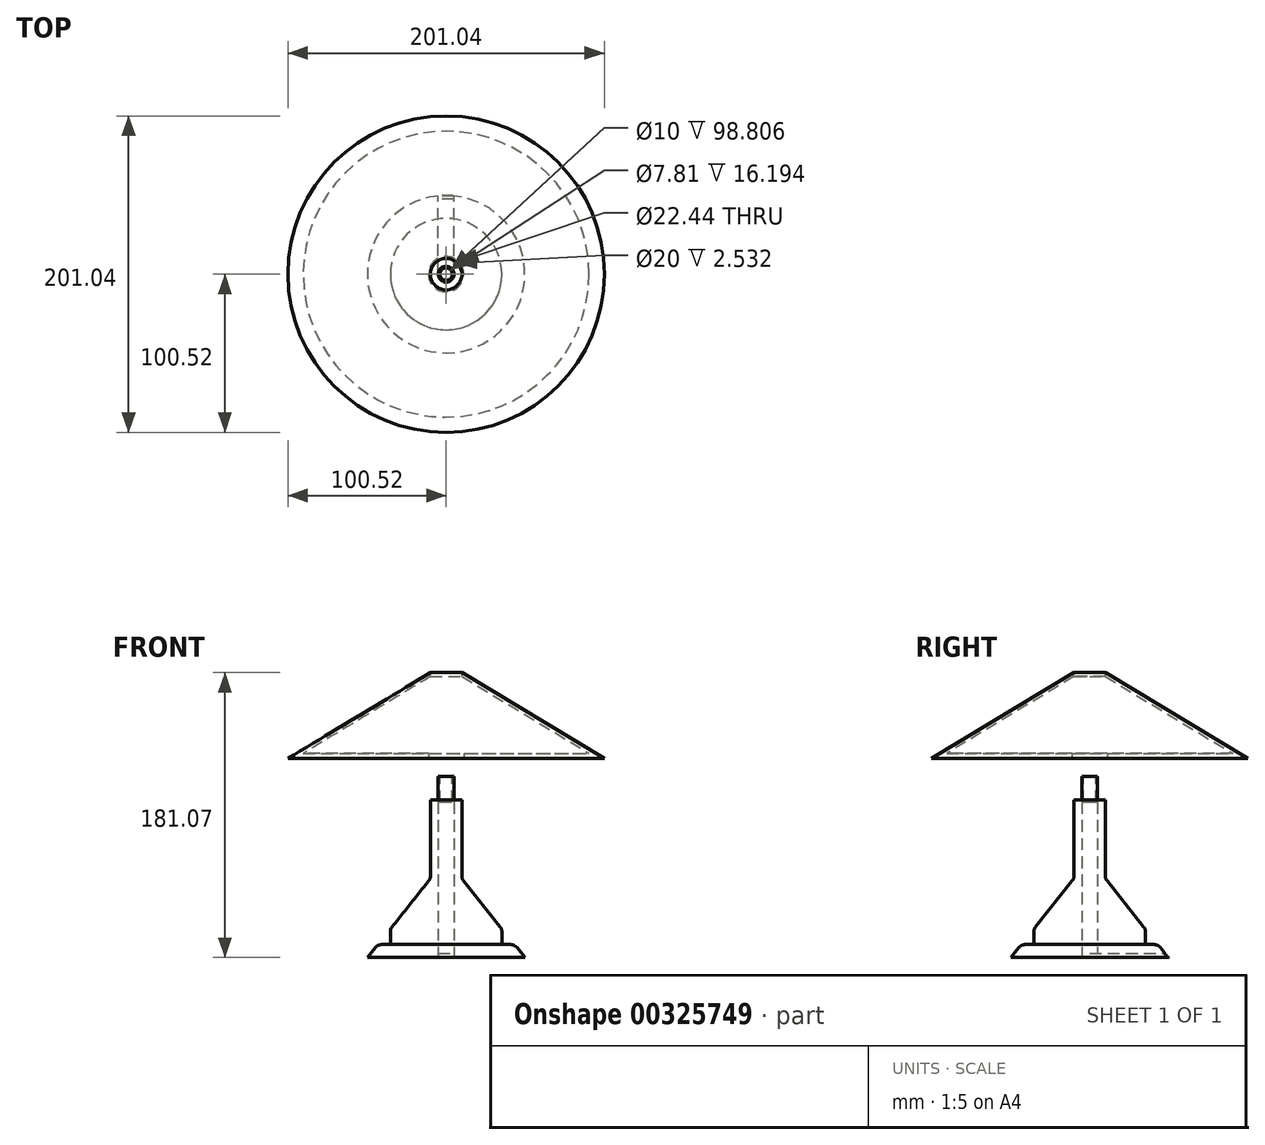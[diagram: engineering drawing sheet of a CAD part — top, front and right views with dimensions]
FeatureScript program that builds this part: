
annotation { "Feature Type Name" : "Feature", "Feature Type Description" : "" }
export const myFeature = defineFeature(function(context is Context, id is Id, definition is map)
    precondition{}
    {
        {
            var Q0;
            Q0=qCreatedBy(makeId("Front.planeOp"),FACE);
            var sketch = newSketch(context, id + "F0", { "sketchPlane" : qUnion([Q0])});
            skLineSegment(sketch, "E0", {"start": v(0, -50) * mm, "end": v(-50, -50) * mm});
            skLineSegment(sketch, "E1", {"start": v(-50, -50) * mm, "end": v(-43.39, -41.73) * mm});
            skLineSegment(sketch, "E2", {"start": v(-10, 0) * mm, "end": v(-10, 50) * mm});
            skLineSegment(sketch, "E3", {"start": v(-10, 50) * mm, "end": v(0, 50) * mm});
            skLineSegment(sketch, "E4", {"start": v(0, 50) * mm, "end": v(0, -50) * mm});
            skLineSegment(sketch, "E5", {"start": v(-5, 50) * mm, "end": v(-5, 65) * mm});
            skLineSegment(sketch, "E6", {"start": v(-5, 65) * mm, "end": v(0, 65) * mm});
            skLineSegment(sketch, "E7", {"start": v(0, 65) * mm, "end": v(0, 50) * mm});
            skLineSegment(sketch, "E8", {"start": v(-43.39, -41.73) * mm, "end": v(-35.4, -41.73) * mm});
            skLineSegment(sketch, "E9", {"start": v(-35.4, -41.73) * mm, "end": v(-35.4, -31.75) * mm});
            skLineSegment(sketch, "E10.trimOffspring", {"start": v(-35.4, -31.75) * mm, "end": v(-10, 0) * mm});
            skSolve(sketch);
        }
        {
            var Q0;
            Q0=qSketchRegion(id+"F0",true);
            var Q1;
            Q1=sQuery(id+"F0.wireOp",EDGE,"E7");
            revolve(context, id + "F1", {"entities" : qUnion([Q0]), "axis" : qUnion([Q1]), "revolveType" : RevolveType.FULL});
        }
        {
            var Q0;
            Q0=makeQuery(id+"F1.opRevolve","SWEPT_FACE",FACE,{"disambiguationData":[OSD([sQuery(id+"F0.wireOp",EDGE,"E0")])]});
            var sketch = newSketch(context, id + "F2", { "sketchPlane" : qUnion([Q0])});
            skCircle(sketch, "E11", {"center": v(0, 0) * mm, "radius": 5 * mm});
            skSolve(sketch);
        }
        {
            var Q0;
            Q0=makeQuery(id+"F2.imprint","IMPRINT",FACE,{"disambiguationData":[TD([[makeQuery(id+"F2.imprint","IMPRINT",EDGE,{"derivedFrom":sQuery(id+"F2.wireOp",EDGE,"E11")}),1.0]])]});
            extrude(context, id + "F3", {"entities" : qUnion([Q0]), "operationType" : NewBodyOperationType.REMOVE, "oppositeDirection" : true, "depth" : 98.8 * mm});
        }
        {
            var Q0;
            Q0=makeQuery(id+"F1.opRevolve","SWEPT_FACE",FACE,{"disambiguationData":[OSD([sQuery(id+"F0.wireOp",EDGE,"E6")])]});
            var sketch = newSketch(context, id + "F4", { "sketchPlane" : qUnion([Q0])});
            skCircle(sketch, "E12", {"center": v(0, 0) * mm, "radius": 3.9 * mm});
            skSolve(sketch);
        }
        {
            var Q0;
            Q0=makeQuery(id+"F4.imprint","IMPRINT",FACE,{"disambiguationData":[TD([[makeQuery(id+"F4.imprint","IMPRINT",EDGE,{"derivedFrom":sQuery(id+"F4.wireOp",EDGE,"E12")}),1.0]])]});
            var Q1;
            Q1=sQuery(id+"F4.wireOp",EDGE,"E12");
            extrude(context, id + "F5", {"entities" : qUnion([Q0]), "operationType" : NewBodyOperationType.REMOVE, "surfaceEntities" : qUnion([Q1]), "oppositeDirection" : true, "depth" : 18.03 * mm});
        }
        {
            var Q0;
            Q0=qCreatedBy(makeId("Front.planeOp"),FACE);
            var sketch = newSketch(context, id + "F6", { "sketchPlane" : qUnion([Q0])});
            skLineSegment(sketch, "E13", {"start": v(0, 81.07) * mm, "end": v(0, 83.72) * mm});
            skLineSegment(sketch, "E14", {"start": v(100.52, 76.39) * mm, "end": v(10, 131.07) * mm});
            skLineSegment(sketch, "E15", {"start": v(0, 131.07) * mm, "end": v(10, 131.07) * mm});
            skLineSegment(sketch, "E16", {"start": v(0, 128.54) * mm, "end": v(10, 128.54) * mm});
            skLineSegment(sketch, "E17", {"start": v(10, 128.54) * mm, "end": v(90.8, 79.72) * mm});
            skLineSegment(sketch, "E18.trimOffspring", {"start": v(0, 128.54) * mm, "end": v(0, 131.07) * mm});
            skLineSegment(sketch, "E19", {"start": v(0, 131.07) * mm, "end": v(0, 81.07) * mm});
            skLineSegment(sketch, "E20", {"start": v(100.52, 76.39) * mm, "end": v(11.22, 76.39) * mm});
            skLineSegment(sketch, "E21", {"start": v(11.22, 76.39) * mm, "end": v(11.22, 79.63) * mm});
            skLineSegment(sketch, "E22", {"start": v(11.22, 79.63) * mm, "end": v(90.8, 79.72) * mm});
            skSolve(sketch);
        }
        {
            var Q0;
            Q0=qSketchRegion(id+"F6",true);
            var Q1;
            Q1=sQuery(id+"F6.wireOp",EDGE,"pKssnT2N-DJuv-aNKx-k4Lw-VZBVBOwzWhS8");
            var Q2;
            Q2=sQuery(id+"F6.wireOp",EDGE,"E16");
            var Q3;
            Q3=sQuery(id+"F6.wireOp",EDGE,"E17");
            var Q4;
            Q4=sQuery(id+"F6.wireOp",EDGE,"MncOqVzV-dVDM-nEzL-s3Sz-IolONIR63Kfi");
            var Q5;
            Q5=sQuery(id+"F6.wireOp",EDGE,"E13");
            revolve(context, id + "F7", {"entities" : qUnion([Q0]), "surfaceEntities" : qUnion([Q1, Q2, Q3, Q4]), "axis" : qUnion([Q5]), "revolveType" : RevolveType.FULL});
        }
        {
            var Q0;
            Q0=makeQuery(id+"F7.opRevolve","SWEPT_FACE",FACE,{"disambiguationData":[OSD([sQuery(id+"F6.wireOp",EDGE,"E15")])]});
            extrude(context, id + "F8", {"entities" : qUnion([Q0]), "operationType" : NewBodyOperationType.REMOVE, "oppositeDirection" : true, "depth" : 55.37 * mm});
        }
        {
            var Q0;
            Q0=makeQuery(id+"F1.opRevolve","SWEPT_EDGE",EDGE,{"disambiguationData":[OSD([sQuery(id+"F0.wireOp",EDGE,"E9"),sQuery(id+"F0.wireOp",EDGE,"E10.trimOffspring")])]});
            var Q1;
            Q1=makeQuery(id+"F1.opRevolve","SWEPT_EDGE",EDGE,{"disambiguationData":[OSD([sQuery(id+"F0.wireOp",EDGE,"E1"),sQuery(id+"F0.wireOp",EDGE,"E8")])]});
            var Q2;
            Q2=makeQuery(id+"F1.opRevolve","SWEPT_FACE",FACE,{"disambiguationData":[OSD([sQuery(id+"F0.wireOp",EDGE,"E10.trimOffspring")])]});
            fillet(context, id + "F9", {"entities" : qUnion([Q0, Q1, Q2]), "radius" : 5.08 * mm, "tangentPropagation" : true, "allowEdgeOverflow" : false});
        }
        {
            var Q0;
            Q0=makeQuery(id+"F1.opRevolve","SWEPT_FACE",FACE,{"disambiguationData":[OSD([sQuery(id+"F0.wireOp",EDGE,"E0")])]});
            var sketch = newSketch(context, id + "F10", { "sketchPlane" : qUnion([Q0])});
            skLineSegment(sketch, "E23", {"start": v(5, 0) * mm, "end": v(5, -49.75) * mm});
            skLineSegment(sketch, "E24", {"start": v(-5, 0) * mm, "end": v(-5, -49.75) * mm});
            skLineSegment(sketch, "E25", {"start": v(5, -49.75) * mm, "end": v(-5, -49.75) * mm});
            skLineSegment(sketch, "E26", {"start": v(5, 0) * mm, "end": v(-5, 0) * mm});
            skSolve(sketch);
        }
        {
            var Q0;
            Q0=qSketchRegion(id+"F10",true);
            extrude(context, id + "F11", {"entities" : qUnion([Q0]), "operationType" : NewBodyOperationType.REMOVE, "oppositeDirection" : true, "depth" : 2.8 * mm});
        }
    });
